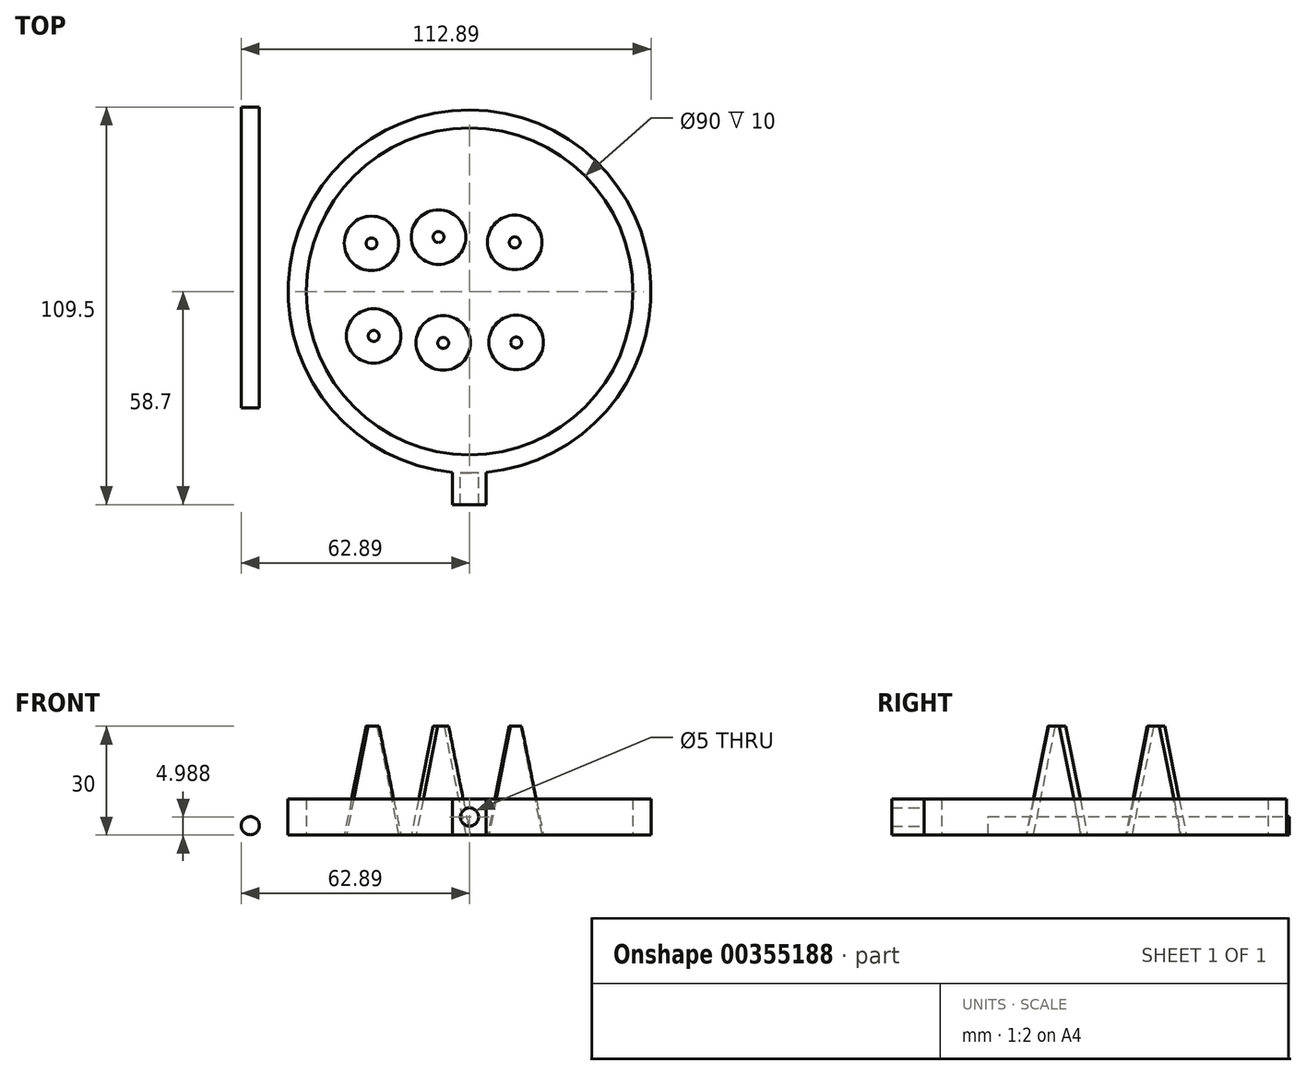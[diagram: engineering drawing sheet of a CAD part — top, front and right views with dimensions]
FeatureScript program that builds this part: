
annotation { "Feature Type Name" : "Feature", "Feature Type Description" : "" }
export const myFeature = defineFeature(function(context is Context, id is Id, definition is map)
    precondition{}
    {
        {
            var Q0;
            Q0=qCreatedBy(makeId("Top.planeOp"),FACE);
            var sketch = newSketch(context, id + "F0", { "sketchPlane" : qUnion([Q0])});
            skCircle(sketch, "E0", {"center": v(0, 0) * mm, "radius": 45 * mm});
            skCircle(sketch, "E1", {"center": v(0, 0) * mm, "radius": 50 * mm});
            skCircle(sketch, "E2", {"center": v(0, 0) * mm, "radius": 2.25 * mm});
            skCircle(sketch, "E3", {"center": v(-26.41, -12.24) * mm, "radius": 7.5 * mm});
            skCircle(sketch, "E4", {"center": v(-7.26, -14.17) * mm, "radius": 7.5 * mm});
            skCircle(sketch, "E5", {"center": v(12.85, -14.04) * mm, "radius": 7.5 * mm});
            skCircle(sketch, "E6", {"center": v(12.45, 13.51) * mm, "radius": 7.5 * mm});
            skCircle(sketch, "E7", {"center": v(-8.54, 14.97) * mm, "radius": 7.5 * mm});
            skCircle(sketch, "E8", {"center": v(-27, 13.25) * mm, "radius": 7.5 * mm});
            skSolve(sketch);
        }
        {
            var Q0;
            Q0=makeQuery(id+"F0.imprint","IMPRINT",FACE,{"disambiguationData":[TD([[makeQuery(id+"F0.imprint","IMPRINT",EDGE,{"derivedFrom":sQuery(id+"F0.wireOp",EDGE,"E0")}),-1.0]])]});
            extrude(context, id + "F1", {"entities" : qUnion([Q0]), "depth" : 10 * mm});
        }
        {
            var Q0;
            Q0=qCreatedBy(makeId("Front.planeOp"),FACE);
            var sketch = newSketch(context, id + "F2", { "sketchPlane" : qUnion([Q0])});
            skCircle(sketch, "E9", {"center": v(0, 4.99) * mm, "radius": 4.5 * mm});
            skCircle(sketch, "E10", {"center": v(0, 4.99) * mm, "radius": 2.5 * mm});
            skLineSegment(sketch, "E11.bottom", {"start": v(-4.69, 10) * mm, "end": v(4.54, 10) * mm});
            skLineSegment(sketch, "E11.top", {"start": v(-4.69, 0) * mm, "end": v(4.54, 0) * mm});
            skLineSegment(sketch, "E11.left", {"start": v(-4.69, 10) * mm, "end": v(-4.69, 0) * mm});
            skLineSegment(sketch, "E11.right", {"start": v(4.54, 10) * mm, "end": v(4.54, 0) * mm});
            skSolve(sketch);
        }
        {
            var Q0;
            Q0=makeQuery(id+"F2.imprint","IMPRINT",FACE,{"disambiguationData":[TD([[makeQuery(id+"F2.imprint","IMPRINT",EDGE,{"derivedFrom":sQuery(id+"F2.wireOp",EDGE,"E9")}),1.0]])]});
            var Q1;
            Q1=makeQuery(id+"F2.imprint","IMPRINT",FACE,{"disambiguationData":[TD([[makeQuery(id+"F2.imprint","IMPRINT",EDGE,{"derivedFrom":sQuery(id+"F2.wireOp",EDGE,"E9")}),-1.0]])]});
            extrude(context, id + "F3", {"entities" : qUnion([Q0, Q1]), "operationType" : NewBodyOperationType.ADD, "depth" : 58.7 * mm, "hasSecondDirection" : true, "secondDirectionOppositeDirection" : false, "secondDirectionDepth" : 49.2 * mm});
        }
        {
            var Q0;
            Q0=qCreatedBy(makeId("Front.planeOp"),FACE);
            var sketch = newSketch(context, id + "F4", { "sketchPlane" : qUnion([Q0])});
            skCircle(sketch, "E12", {"center": v(-60.39, 2.6) * mm, "radius": 2.5 * mm});
            skSolve(sketch);
        }
        {
            var Q0;
            Q0=makeQuery(id+"F4.imprint","IMPRINT",FACE,{"disambiguationData":[TD([[makeQuery(id+"F4.imprint","IMPRINT",EDGE,{"derivedFrom":sQuery(id+"F4.wireOp",EDGE,"E12")}),1.0]])]});
            extrude(context, id + "F5", {"entities" : qUnion([Q0]), "depth" : 32.1 * mm, "hasSecondDirection" : true, "secondDirectionOppositeDirection" : true, "secondDirectionDepth" : 50.8 * mm});
        }
        {
            var Q0;
            Q0=makeQuery(id+"F0.imprint","IMPRINT",FACE,{"disambiguationData":[TD([[makeQuery(id+"F0.imprint","IMPRINT",EDGE,{"derivedFrom":sQuery(id+"F0.wireOp",EDGE,"E3")}),1.0]])]});
            var Q1;
            Q1=makeQuery(id+"F0.imprint","IMPRINT",FACE,{"disambiguationData":[TD([[makeQuery(id+"F0.imprint","IMPRINT",EDGE,{"derivedFrom":sQuery(id+"F0.wireOp",EDGE,"E8")}),1.0]])]});
            var Q2;
            Q2=makeQuery(id+"F0.imprint","IMPRINT",FACE,{"disambiguationData":[TD([[makeQuery(id+"F0.imprint","IMPRINT",EDGE,{"derivedFrom":sQuery(id+"F0.wireOp",EDGE,"E7")}),1.0]])]});
            var Q3;
            Q3=makeQuery(id+"F0.imprint","IMPRINT",FACE,{"disambiguationData":[TD([[makeQuery(id+"F0.imprint","IMPRINT",EDGE,{"derivedFrom":sQuery(id+"F0.wireOp",EDGE,"E6")}),1.0]])]});
            var Q4;
            Q4=makeQuery(id+"F0.imprint","IMPRINT",FACE,{"disambiguationData":[TD([[makeQuery(id+"F0.imprint","IMPRINT",EDGE,{"derivedFrom":sQuery(id+"F0.wireOp",EDGE,"E4")}),1.0]])]});
            var Q5;
            Q5=makeQuery(id+"F0.imprint","IMPRINT",FACE,{"disambiguationData":[TD([[makeQuery(id+"F0.imprint","IMPRINT",EDGE,{"derivedFrom":sQuery(id+"F0.wireOp",EDGE,"E5")}),1.0]])]});
            extrude(context, id + "F6", {"entities" : qUnion([Q0, Q1, Q2, Q3, Q4, Q5]), "depth" : 30 * mm});
        }
        {
            var Q0;
            Q0=makeQuery(id+"F6.opExtrude","CAP_EDGE",EDGE,{"disambiguationData":[OSD([sQuery(id+"F0.wireOp",EDGE,"E3")])],"isStart":false});
            var Q1;
            Q1=makeQuery(id+"F6.opExtrude","CAP_EDGE",EDGE,{"disambiguationData":[OSD([sQuery(id+"F0.wireOp",EDGE,"E4")])],"isStart":false});
            var Q2;
            Q2=makeQuery(id+"F6.opExtrude","CAP_EDGE",EDGE,{"disambiguationData":[OSD([sQuery(id+"F0.wireOp",EDGE,"E5")])],"isStart":false});
            var Q3;
            Q3=makeQuery(id+"F6.opExtrude","CAP_EDGE",EDGE,{"disambiguationData":[OSD([sQuery(id+"F0.wireOp",EDGE,"E6")])],"isStart":false});
            var Q4;
            Q4=makeQuery(id+"F6.opExtrude","CAP_EDGE",EDGE,{"disambiguationData":[OSD([sQuery(id+"F0.wireOp",EDGE,"E7")])],"isStart":false});
            var Q5;
            Q5=makeQuery(id+"F6.opExtrude","CAP_EDGE",EDGE,{"disambiguationData":[OSD([sQuery(id+"F0.wireOp",EDGE,"E8")])],"isStart":false});
            chamfer(context, id + "F7", {"entities" : qUnion([Q0, Q1, Q2, Q3, Q4, Q5]), "chamferType" : ChamferType.TWO_OFFSETS, "width1" : 6 * mm, "oppositeDirection" : false, "width2" : 30 * mm, "tangentPropagation" : true});
        }
    });
